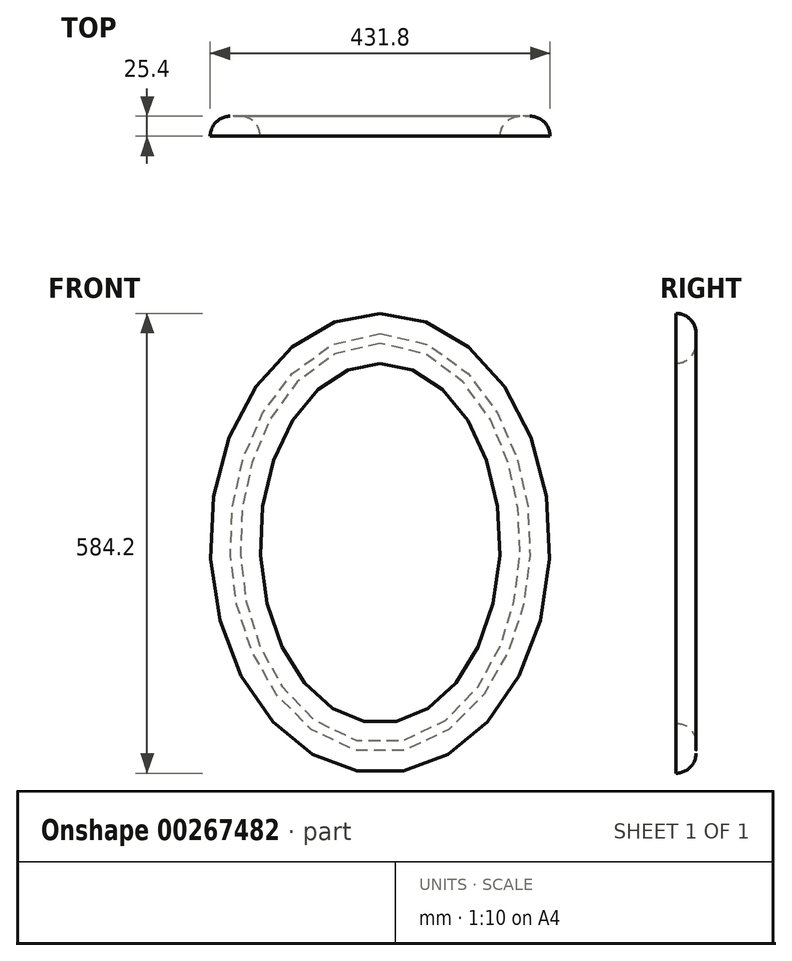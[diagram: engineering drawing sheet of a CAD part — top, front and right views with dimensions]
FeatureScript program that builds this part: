
annotation { "Feature Type Name" : "Feature", "Feature Type Description" : "" }
export const myFeature = defineFeature(function(context is Context, id is Id, definition is map)
    precondition{}
    {
        {
            var Q0;
            Q0=qCreatedBy(makeId("Front.planeOp"),FACE);
            var sketch = newSketch(context, id + "F0", { "sketchPlane" : qUnion([Q0])});
            skEllipse(sketch, "E0", {"center": v(0, 0) * mm, "majorRadius": 228.6 * mm, "minorRadius": 152.4 * mm, "majorAxis": v(0, 1)});
            skEllipse(sketch, "E1", {"center": v(0, 0) * mm, "majorRadius": 292.1 * mm, "minorRadius": 215.9 * mm, "majorAxis": v(0, 1)});
            skSolve(sketch);
        }
        {
            var Q0;
            Q0=makeQuery(id+"F0.imprint","IMPRINT",FACE,{"disambiguationData":[TD([[makeQuery(id+"F0.imprint","IMPRINT",EDGE,{"derivedFrom":sQuery(id+"F0.wireOp",EDGE,"E0")}),-1.0]])]});
            extrude(context, id + "F1", {"entities" : qUnion([Q0]), "oppositeDirection" : true, "depth" : 25.4 * mm});
        }
        {
            var Q0;
            Q0=makeQuery(id+"F1.opExtrude","CAP_EDGE",EDGE,{"disambiguationData":[OSD([sQuery(id+"F0.wireOp",EDGE,"E0")])],"isStart":false});
            fillet(context, id + "F2", {"entities" : qUnion([Q0]), "radius" : 25.4 * mm, "tangentPropagation" : true, "allowEdgeOverflow" : false});
        }
        {
            var Q0;
            Q0=makeQuery(id+"F1.opExtrude","CAP_EDGE",EDGE,{"disambiguationData":[OSD([sQuery(id+"F0.wireOp",EDGE,"E1")])],"isStart":false});
            fillet(context, id + "F3", {"entities" : qUnion([Q0]), "radius" : 25.4 * mm, "tangentPropagation" : true, "allowEdgeOverflow" : false});
        }
    });
